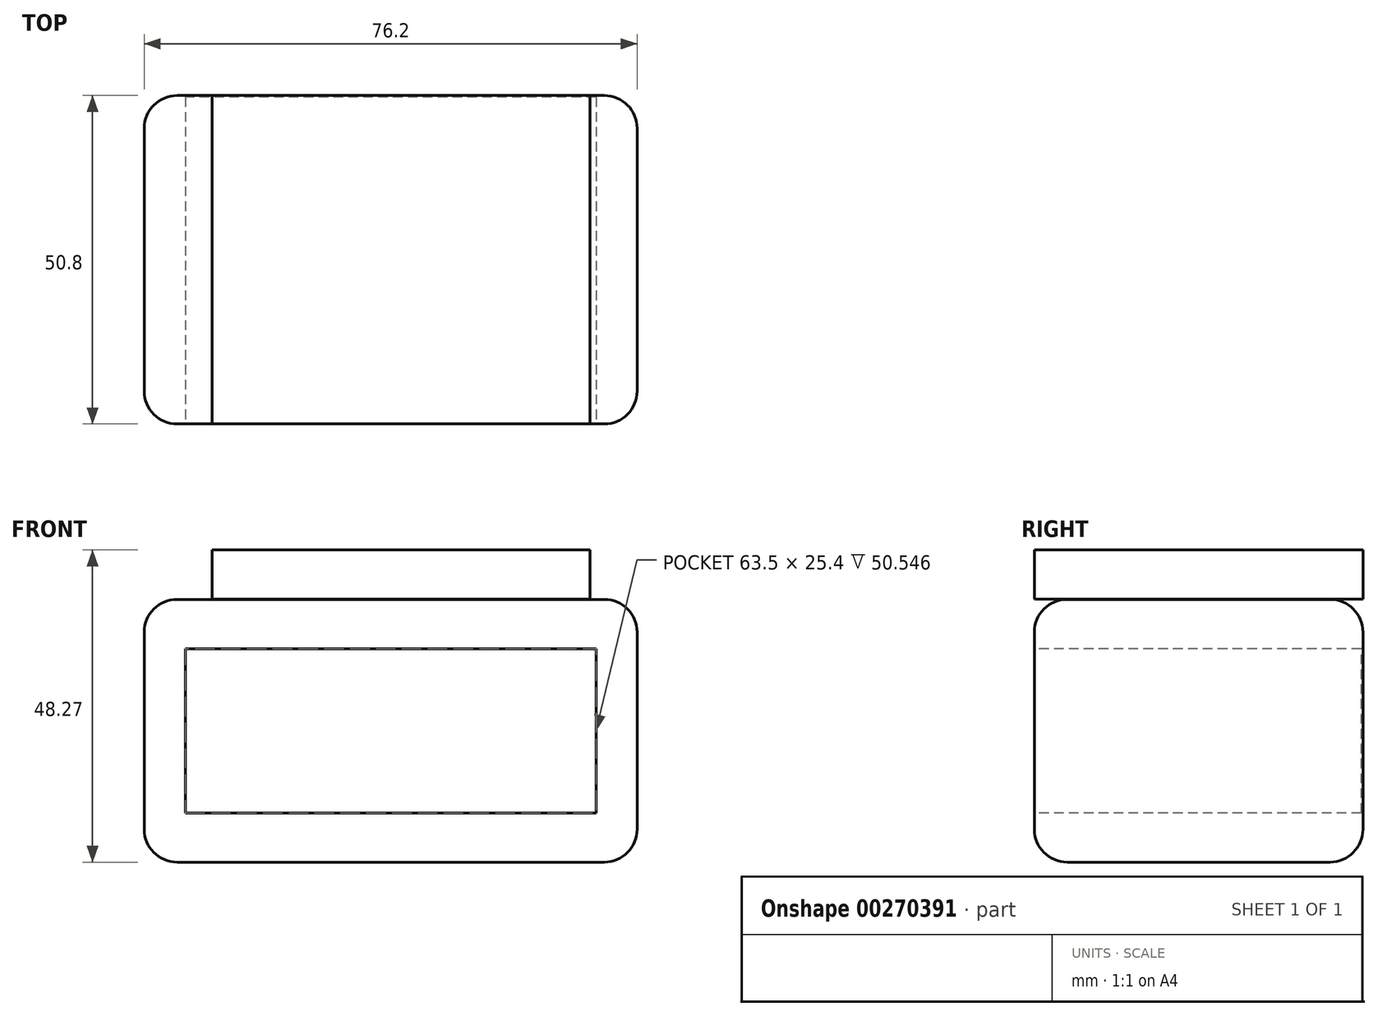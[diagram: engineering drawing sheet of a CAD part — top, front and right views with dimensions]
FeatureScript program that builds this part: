
annotation { "Feature Type Name" : "Feature", "Feature Type Description" : "" }
export const myFeature = defineFeature(function(context is Context, id is Id, definition is map)
    precondition{}
    {
        {
            var Q0;
            Q0=qCreatedBy(makeId("Front.planeOp"),FACE);
            var sketch = newSketch(context, id + "F0", { "sketchPlane" : qUnion([Q0])});
            skLineSegment(sketch, "E0.bottom", {"start": v(38.1, -20.32) * mm, "end": v(-38.1, -20.32) * mm});
            skLineSegment(sketch, "E0.top", {"start": v(38.1, 20.32) * mm, "end": v(-38.1, 20.32) * mm});
            skLineSegment(sketch, "E0.left", {"start": v(38.1, -20.32) * mm, "end": v(38.1, 20.32) * mm});
            skLineSegment(sketch, "E0.right", {"start": v(-38.1, -20.32) * mm, "end": v(-38.1, 20.32) * mm});
            skPoint(sketch, "E0.middle", {"position": v(0, 0) * mm});
            skSolve(sketch);
        }
        {
            var Q0;
            Q0=makeQuery(id+"F0.imprint","IMPRINT",FACE,{"disambiguationData":[TD([[makeQuery(id+"F0.imprint","IMPRINT",EDGE,{"derivedFrom":sQuery(id+"F0.wireOp",EDGE,"E0.bottom")}),-1.0]])]});
            extrude(context, id + "F1", {"entities" : qUnion([Q0]), "depth" : 50.8 * mm});
        }
        {
            var Q0;
            Q0=makeQuery(id+"F1.opExtrude","CAP_FACE",FACE,{"disambiguationData":[OSD([sQuery(id+"F0.wireOp",EDGE,"E0.bottom"),sQuery(id+"F0.wireOp",EDGE,"E0.top"),sQuery(id+"F0.wireOp",EDGE,"E0.left"),sQuery(id+"F0.wireOp",EDGE,"E0.right")])],"isStart":false});
            var sketch = newSketch(context, id + "F2", { "sketchPlane" : qUnion([Q0])});
            skLineSegment(sketch, "E1.bottom", {"start": v(31.75, -12.7) * mm, "end": v(-31.75, -12.7) * mm});
            skLineSegment(sketch, "E1.top", {"start": v(31.75, 12.7) * mm, "end": v(-31.75, 12.7) * mm});
            skLineSegment(sketch, "E1.left", {"start": v(31.75, -12.7) * mm, "end": v(31.75, 12.7) * mm});
            skLineSegment(sketch, "E1.right", {"start": v(-31.75, -12.7) * mm, "end": v(-31.75, 12.7) * mm});
            skPoint(sketch, "E1.middle", {"position": v(0, 0) * mm});
            skSolve(sketch);
        }
        {
            var Q0;
            Q0=makeQuery(id+"F2.imprint","IMPRINT",FACE,{"disambiguationData":[TD([[makeQuery(id+"F2.imprint","IMPRINT",EDGE,{"derivedFrom":sQuery(id+"F2.wireOp",EDGE,"E1.bottom")}),-1.0]])]});
            extrude(context, id + "F3", {"entities" : qUnion([Q0]), "operationType" : NewBodyOperationType.REMOVE, "oppositeDirection" : true, "depth" : 50.55 * mm});
        }
        {
            var Q0;
            Q0=qCreatedBy(makeId("Front.planeOp"),FACE);
            var sketch = newSketch(context, id + "F4", { "sketchPlane" : qUnion([Q0])});
            skLineSegment(sketch, "E2.bottom", {"start": v(-27.63, 20.33) * mm, "end": v(30.8, 20.33) * mm});
            skLineSegment(sketch, "E2.top", {"start": v(-27.63, 27.95) * mm, "end": v(30.8, 27.95) * mm});
            skLineSegment(sketch, "E2.left", {"start": v(-27.63, 20.33) * mm, "end": v(-27.63, 27.95) * mm});
            skLineSegment(sketch, "E2.right", {"start": v(30.8, 20.33) * mm, "end": v(30.8, 27.95) * mm});
            skSolve(sketch);
        }
        {
            var Q0;
            Q0=makeQuery(id+"F4.imprint","IMPRINT",FACE,{"disambiguationData":[TD([[makeQuery(id+"F4.imprint","IMPRINT",EDGE,{"derivedFrom":sQuery(id+"F4.wireOp",EDGE,"E2.bottom")}),1.0]])]});
            extrude(context, id + "F5", {"entities" : qUnion([Q0]), "depth" : 50.8 * mm});
        }
        {
            var Q0;
            Q0=makeQuery(id+"F1.opExtrude","CAP_EDGE",EDGE,{"disambiguationData":[OSD([sQuery(id+"F0.wireOp",EDGE,"E0.right")])],"isStart":false});
            var Q1;
            Q1=makeQuery(id+"F1.opExtrude","CAP_EDGE",EDGE,{"disambiguationData":[OSD([sQuery(id+"F0.wireOp",EDGE,"E0.top")])],"isStart":false});
            var Q2;
            Q2=makeQuery(id+"F1.opExtrude","CAP_EDGE",EDGE,{"disambiguationData":[OSD([sQuery(id+"F0.wireOp",EDGE,"E0.left")])],"isStart":false});
            var Q3;
            Q3=makeQuery(id+"F1.opExtrude","CAP_EDGE",EDGE,{"disambiguationData":[OSD([sQuery(id+"F0.wireOp",EDGE,"E0.bottom")])],"isStart":false});
            var Q4;
            Q4=makeQuery(id+"F1.opExtrude","SWEPT_EDGE",EDGE,{"disambiguationData":[OSD([sQuery(id+"F0.wireOp",EDGE,"E0.top"),sQuery(id+"F0.wireOp",EDGE,"E0.left")])]});
            var Q5;
            Q5=makeQuery(id+"F1.opExtrude","CAP_EDGE",EDGE,{"disambiguationData":[OSD([sQuery(id+"F0.wireOp",EDGE,"E0.left")])],"isStart":true});
            var Q6;
            Q6=makeQuery(id+"F1.opExtrude","SWEPT_EDGE",EDGE,{"disambiguationData":[OSD([sQuery(id+"F0.wireOp",EDGE,"E0.bottom"),sQuery(id+"F0.wireOp",EDGE,"E0.left")])]});
            var Q7;
            Q7=makeQuery(id+"F1.opExtrude","SWEPT_EDGE",EDGE,{"disambiguationData":[OSD([sQuery(id+"F0.wireOp",EDGE,"E0.top"),sQuery(id+"F0.wireOp",EDGE,"E0.right")])]});
            var Q8;
            Q8=makeQuery(id+"F1.opExtrude","CAP_EDGE",EDGE,{"disambiguationData":[OSD([sQuery(id+"F0.wireOp",EDGE,"E0.top")])],"isStart":true});
            var Q9;
            Q9=makeQuery(id+"F1.opExtrude","SWEPT_EDGE",EDGE,{"disambiguationData":[OSD([sQuery(id+"F0.wireOp",EDGE,"E0.bottom"),sQuery(id+"F0.wireOp",EDGE,"E0.right")])]});
            var Q10;
            Q10=makeQuery(id+"F1.opExtrude","CAP_EDGE",EDGE,{"disambiguationData":[OSD([sQuery(id+"F0.wireOp",EDGE,"E0.right")])],"isStart":true});
            var Q11;
            Q11=makeQuery(id+"F1.opExtrude","CAP_EDGE",EDGE,{"disambiguationData":[OSD([sQuery(id+"F0.wireOp",EDGE,"E0.bottom")])],"isStart":true});
            fillet(context, id + "F6", {"entities" : qUnion([Q0, Q1, Q2, Q3, Q4, Q5, Q6, Q7, Q8, Q9, Q10, Q11]), "radius" : 5.08 * mm, "tangentPropagation" : true, "allowEdgeOverflow" : false});
        }
    });
